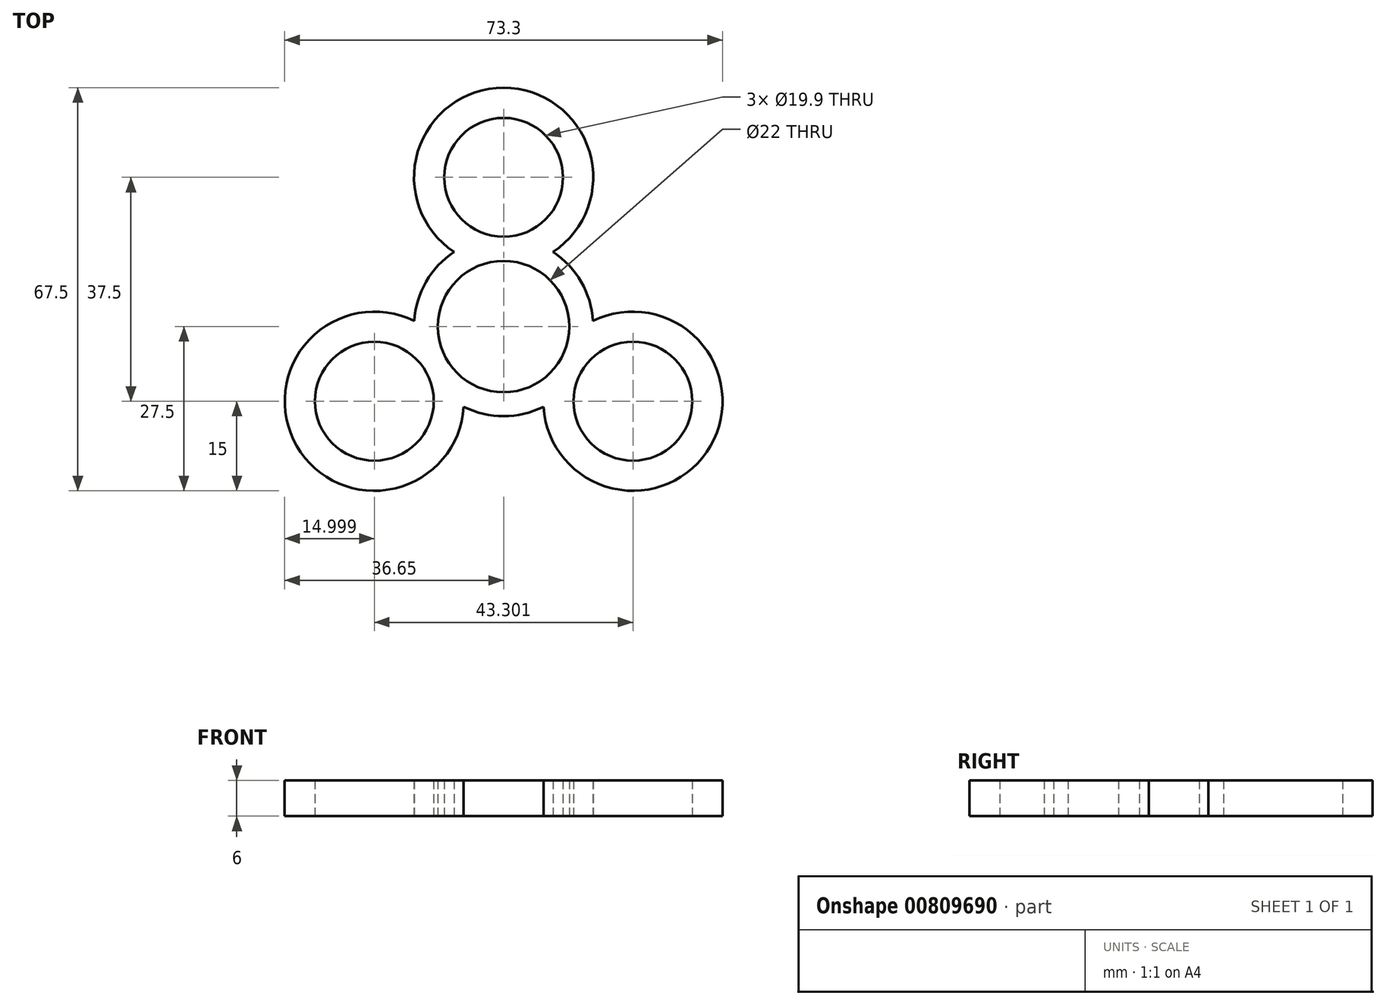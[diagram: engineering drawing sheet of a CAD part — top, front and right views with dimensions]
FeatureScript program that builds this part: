
annotation { "Feature Type Name" : "Feature", "Feature Type Description" : "" }
export const myFeature = defineFeature(function(context is Context, id is Id, definition is map)
    precondition{}
    {
        {
            var Q0;
            Q0=qCreatedBy(makeId("Top.planeOp"),FACE);
            var sketch = newSketch(context, id + "F0", { "sketchPlane" : qUnion([Q0])});
            skSolve(sketch);
        }
        {
            var Q0;
            Q0=qCreatedBy(makeId("Top.planeOp"),FACE);
            var sketch = newSketch(context, id + "F1", { "sketchPlane" : qUnion([Q0])});
            skArc(sketch, "E0", {"start": v(9.53, 5.5) * mm, "mid": v(0, 11) * mm, "end": v(-9.53, 5.5) * mm});
            skCircle(sketch, "E1", {"center": v(0, 25) * mm, "radius": 9.95 * mm});
            skArc(sketch, "E2", {"start": v(-8.3, 12.5) * mm, "mid": v(-10.93, 10.27) * mm, "end": v(-13, 7.5) * mm});
            skArc(sketch, "E3.trimOffspring", {"start": v(13, 7.5) * mm, "mid": v(10.93, 10.27) * mm, "end": v(8.3, 12.5) * mm});
            skArc(sketch, "E4.trimOffspring", {"start": v(8.3, 12.5) * mm, "mid": v(0, 40) * mm, "end": v(-8.3, 12.5) * mm});
            skArc(sketch, "E5.1.0", {"start": v(-14.97, 0.93) * mm, "mid": v(-34.64, -20) * mm, "end": v(-6.68, -13.43) * mm});
            skCircle(sketch, "E5.1.1", {"center": v(-21.65, -12.5) * mm, "radius": 9.95 * mm});
            skArc(sketch, "E5.1.2", {"start": v(-6.68, -13.43) * mm, "mid": v(-3.43, -14.6) * mm, "end": v(0, -15) * mm});
            skArc(sketch, "E5.2.0", {"start": v(6.68, -13.43) * mm, "mid": v(34.64, -20) * mm, "end": v(14.97, 0.93) * mm});
            skCircle(sketch, "E5.2.1", {"center": v(21.65, -12.5) * mm, "radius": 9.95 * mm});
            skArc(sketch, "E5.2.2", {"start": v(14.97, 0.93) * mm, "mid": v(14.36, 4.33) * mm, "end": v(13, 7.5) * mm});
            skArc(sketch, "E6.1.1", {"start": v(-13, 7.5) * mm, "mid": v(-14.36, 4.33) * mm, "end": v(-14.97, 0.93) * mm});
            skArc(sketch, "E6.2.1", {"start": v(0, -15) * mm, "mid": v(3.43, -14.6) * mm, "end": v(6.68, -13.43) * mm});
            skArc(sketch, "E7.1.0", {"start": v(-9.53, 5.5) * mm, "mid": v(-9.53, -5.5) * mm, "end": v(0, -11) * mm});
            skArc(sketch, "E7.2.0", {"start": v(0, -11) * mm, "mid": v(9.53, -5.5) * mm, "end": v(9.53, 5.5) * mm});
            skSolve(sketch);
        }
        {
            var Q0;
            Q0 = qSketchRegion(id + "F1", true);
            var Q1;
            Q1 = qSketchRegion(id + "F0", true);
            extrude(context, id + "F2", {"entities" : qUnion([Q0, Q1]), "depth" : 6 * mm, "offsetDistance" : 25 * mm});
        }
    });
